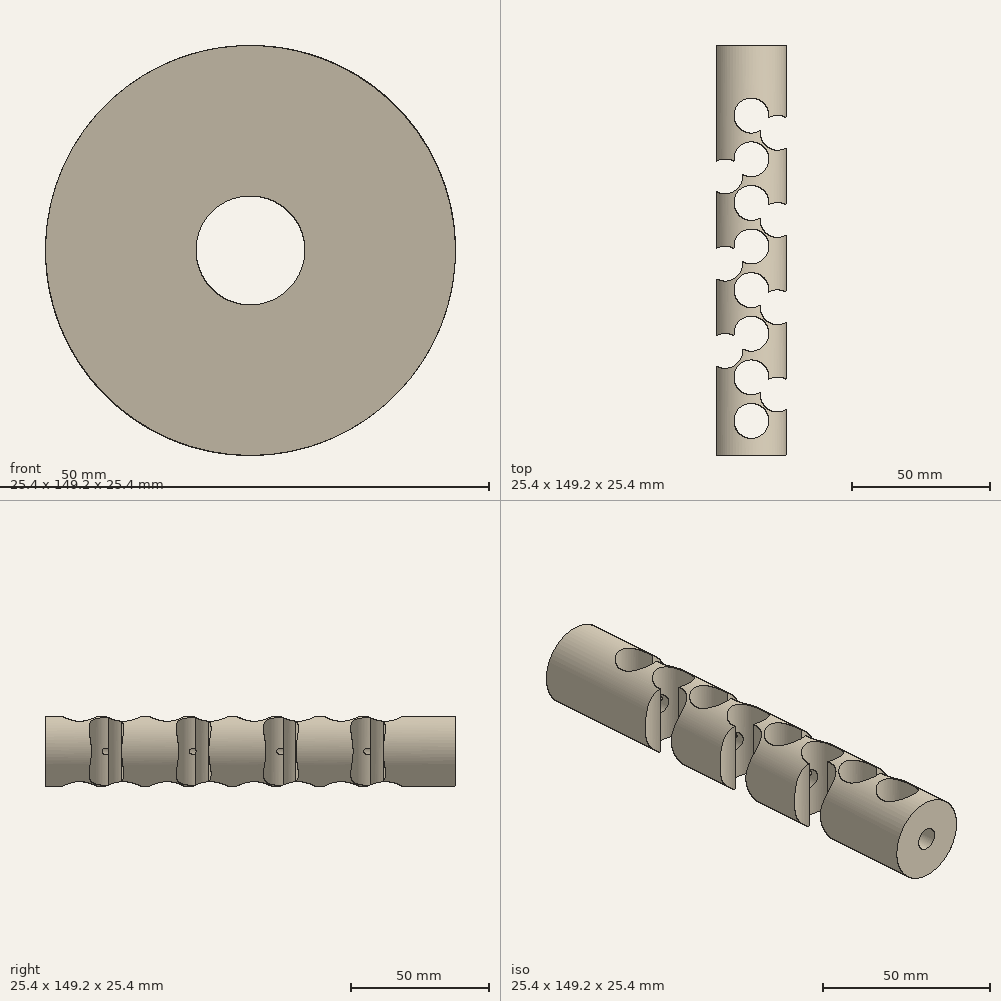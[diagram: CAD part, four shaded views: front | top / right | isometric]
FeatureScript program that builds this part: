
annotation { "Feature Type Name" : "Feature", "Feature Type Description" : "" }
export const myFeature = defineFeature(function(context is Context, id is Id, definition is map)
    precondition{}
    {
        {
            var Q0;
            Q0=qCreatedBy(makeId("Front.planeOp"),FACE);
            var sketch = newSketch(context, id + "F0", { "sketchPlane" : qUnion([Q0])});
            skCircle(sketch, "E0", {"center": v(0, 0) * mm, "radius": 12.7 * mm});
            skSolve(sketch);
        }
        {
            var Q0;
            Q0=makeQuery(id+"F0.imprint","IMPRINT",FACE,{"disambiguationData":[TD([[makeQuery(id+"F0.imprint","IMPRINT",EDGE,{"derivedFrom":sQuery(id+"F0.wireOp",EDGE,"E0")}),1.0]])]});
            extrude(context, id + "F1", {"entities" : qUnion([Q0]), "endBound" : BoundingType.SYMMETRIC, "depth" : 149.22 * mm, "offsetDistance" : 25.4 * mm});
        }
        {
            var Q0;
            Q0=makeQuery(id+"F1.opExtrude","CAP_FACE",FACE,{"disambiguationData":[OSD([sQuery(id+"F0.wireOp",EDGE,"E0")])],"isStart":false});
            var sketch = newSketch(context, id + "F2", { "sketchPlane" : qUnion([Q0])});
            skPoint(sketch, "E1", {"position": v(0, 0) * mm});
            skSolve(sketch);
        }
        {
            var Q0;
            Q0=sQuery(id+"F2.wireOp",VERTEX,"E1");
            var Q1;
            Q1=makeQuery(id+"F1.opExtrude","SWEPT_BODY",BODY,{"disambiguationData":[OSD([sQuery(id+"F0.wireOp",EDGE,"E0")])]});
            hole(context, id + "F3", {"style" : HoleStyle.SIMPLE, "endStyle" : HoleEndStyle.THROUGH, "holeDiameter" : 6.75 * mm, "majorDiameter" : 6.35 * mm, "isTappedThrough" : true, "tappedDepth" : 12.7 * mm, "tapClearance" : 3, "locations" : qUnion([Q0]), "scope" : qUnion([Q1])});
        }
        {
            var Q0;
            Q0=qCreatedBy(makeId("Top.planeOp"),FACE);
            var sketch = newSketch(context, id + "F4", { "sketchPlane" : qUnion([Q0])});
            skLineSegment(sketch, "E2", {"start": v(0, 74.46) * mm, "end": v(0, 49.06) * mm});
            skLineSegment(sketch, "E3", {"start": v(0, 49.06) * mm, "end": v(0, 33.19) * mm});
            skLineSegment(sketch, "E4", {"start": v(0, 33.19) * mm, "end": v(0, 17.31) * mm});
            skLineSegment(sketch, "E5", {"start": v(0, 17.31) * mm, "end": v(0, 1.44) * mm});
            skLineSegment(sketch, "E6", {"start": v(0, 1.44) * mm, "end": v(0, -14.44) * mm});
            skLineSegment(sketch, "E7", {"start": v(0, -14.44) * mm, "end": v(0, -30.31) * mm});
            skLineSegment(sketch, "E8", {"start": v(0, -30.31) * mm, "end": v(0, -46.19) * mm});
            skLineSegment(sketch, "E9", {"start": v(0, -46.19) * mm, "end": v(0, -62.06) * mm});
            skLineSegment(sketch, "E10", {"start": v(0, -62.06) * mm, "end": v(0, -74.72) * mm});
            skSolve(sketch);
        }
        {
            var Q0;
            Q0=sQuery(id+"F4.wireOp",VERTEX,"E9.end");
            var Q1;
            Q1=sQuery(id+"F4.wireOp",VERTEX,"E8.end");
            var Q2;
            Q2=sQuery(id+"F4.wireOp",VERTEX,"E7.end");
            var Q3;
            Q3=sQuery(id+"F4.wireOp",VERTEX,"E6.end");
            var Q4;
            Q4=sQuery(id+"F4.wireOp",VERTEX,"E5.end");
            var Q5;
            Q5=sQuery(id+"F4.wireOp",VERTEX,"E4.end");
            var Q6;
            Q6=sQuery(id+"F4.wireOp",VERTEX,"E3.end");
            var Q7;
            Q7=sQuery(id+"F4.wireOp",VERTEX,"E2.end");
            var Q8;
            Q8=makeQuery(id+"F1.opExtrude","SWEPT_BODY",BODY,{"disambiguationData":[OSD([sQuery(id+"F0.wireOp",EDGE,"E0")])]});
            hole(context, id + "F5", {"style" : HoleStyle.SIMPLE, "endStyle" : HoleEndStyle.BLIND, "holeDiameter" : 12.7 * mm, "majorDiameter" : 6.35 * mm, "holeDepth" : 12.7 * mm, "isTappedThrough" : true, "tappedDepth" : 12.7 * mm, "tapClearance" : 3, "startFromSketch" : true, "locations" : qUnion([Q0, Q1, Q2, Q3, Q4, Q5, Q6, Q7]), "scope" : qUnion([Q8])});
        }
        {
            var Q0;
            Q0=sQuery(id+"F4.wireOp",VERTEX,"E9.end");
            var Q1;
            Q1=sQuery(id+"F4.wireOp",VERTEX,"E8.end");
            var Q2;
            Q2=sQuery(id+"F4.wireOp",VERTEX,"E7.end");
            var Q3;
            Q3=sQuery(id+"F4.wireOp",VERTEX,"E6.end");
            var Q4;
            Q4=sQuery(id+"F4.wireOp",VERTEX,"E5.end");
            var Q5;
            Q5=sQuery(id+"F4.wireOp",VERTEX,"E4.end");
            var Q6;
            Q6=sQuery(id+"F4.wireOp",VERTEX,"E3.end");
            var Q7;
            Q7=sQuery(id+"F4.wireOp",VERTEX,"E2.end");
            var Q8;
            Q8=makeQuery(id+"F1.opExtrude","SWEPT_BODY",BODY,{"disambiguationData":[OSD([sQuery(id+"F0.wireOp",EDGE,"E0")])]});
            hole(context, id + "F6", {"style" : HoleStyle.SIMPLE, "endStyle" : HoleEndStyle.BLIND, "oppositeDirection" : true, "holeDiameter" : 12.7 * mm, "majorDiameter" : 6.35 * mm, "holeDepth" : 12.7 * mm, "isTappedThrough" : true, "tappedDepth" : 12.7 * mm, "tapClearance" : 3, "startFromSketch" : true, "locations" : qUnion([Q0, Q1, Q2, Q3, Q4, Q5, Q6, Q7]), "scope" : qUnion([Q8])});
        }
        {
            var Q0;
            Q0=qCreatedBy(makeId("Top.planeOp"),FACE);
            var sketch = newSketch(context, id + "F7", { "sketchPlane" : qUnion([Q0])});
            skLineSegment(sketch, "E11", {"start": v(0, 49.18) * mm, "end": v(9.53, 49.18) * mm});
            skLineSegment(sketch, "E12", {"start": v(9.53, 49.18) * mm, "end": v(9.53, 42.83) * mm});
            skPoint(sketch, "E13", {"position": v(9.53, 42.83) * mm});
            skLineSegment(sketch, "E14", {"start": v(9.53, 42.83) * mm, "end": v(9.53, 26.95) * mm});
            skLineSegment(sketch, "E15", {"start": v(9.53, 26.95) * mm, "end": v(9.53, 11.08) * mm});
            skLineSegment(sketch, "E16", {"start": v(9.53, 11.08) * mm, "end": v(9.53, -4.8) * mm});
            skLineSegment(sketch, "E17", {"start": v(9.53, -4.8) * mm, "end": v(9.53, -20.67) * mm});
            skLineSegment(sketch, "E18", {"start": v(9.53, -20.67) * mm, "end": v(9.53, -36.55) * mm});
            skLineSegment(sketch, "E19", {"start": v(9.53, -36.55) * mm, "end": v(9.53, -52.42) * mm});
            skLineSegment(sketch, "E20", {"start": v(9.53, 26.95) * mm, "end": v(-9.52, 26.95) * mm});
            skLineSegment(sketch, "E21", {"start": v(9.53, -4.8) * mm, "end": v(-9.52, -4.8) * mm});
            skLineSegment(sketch, "E22", {"start": v(9.53, -36.55) * mm, "end": v(-9.52, -36.55) * mm});
            skSolve(sketch);
        }
        {
            var Q0;
            Q0=sQuery(id+"F7.wireOp",VERTEX,"E13");
            var Q1;
            Q1=sQuery(id+"F7.wireOp",VERTEX,"E15.end");
            var Q2;
            Q2=sQuery(id+"F7.wireOp",VERTEX,"E17.end");
            var Q3;
            Q3=sQuery(id+"F7.wireOp",VERTEX,"E19.end");
            var Q4;
            Q4=makeQuery(id+"F1.opExtrude","SWEPT_BODY",BODY,{"disambiguationData":[OSD([sQuery(id+"F0.wireOp",EDGE,"E0")])]});
            hole(context, id + "F8", {"style" : HoleStyle.SIMPLE, "endStyle" : HoleEndStyle.BLIND, "oppositeDirection" : true, "holeDiameter" : 12.7 * mm, "majorDiameter" : 6.35 * mm, "holeDepth" : 12.7 * mm, "isTappedThrough" : true, "tappedDepth" : 12.7 * mm, "tapClearance" : 3, "startFromSketch" : true, "locations" : qUnion([Q0, Q1, Q2, Q3]), "scope" : qUnion([Q4])});
        }
        {
            var Q0;
            Q0=sQuery(id+"F7.wireOp",VERTEX,"E13");
            var Q1;
            Q1=sQuery(id+"F7.wireOp",VERTEX,"E15.end");
            var Q2;
            Q2=sQuery(id+"F7.wireOp",VERTEX,"E17.end");
            var Q3;
            Q3=sQuery(id+"F7.wireOp",VERTEX,"E19.end");
            var Q4;
            Q4=makeQuery(id+"F1.opExtrude","SWEPT_BODY",BODY,{"disambiguationData":[OSD([sQuery(id+"F0.wireOp",EDGE,"E0")])]});
            hole(context, id + "F9", {"style" : HoleStyle.SIMPLE, "endStyle" : HoleEndStyle.BLIND, "holeDiameter" : 12.7 * mm, "majorDiameter" : 6.35 * mm, "holeDepth" : 12.7 * mm, "isTappedThrough" : true, "tappedDepth" : 12.7 * mm, "tapClearance" : 3, "startFromSketch" : true, "locations" : qUnion([Q0, Q1, Q2, Q3]), "scope" : qUnion([Q4])});
        }
        {
            var Q0;
            Q0=sQuery(id+"F7.wireOp",VERTEX,"E20.end");
            var Q1;
            Q1=sQuery(id+"F7.wireOp",VERTEX,"E21.end");
            var Q2;
            Q2=sQuery(id+"F7.wireOp",VERTEX,"E22.end");
            var Q3;
            Q3=makeQuery(id+"F1.opExtrude","SWEPT_BODY",BODY,{"disambiguationData":[OSD([sQuery(id+"F0.wireOp",EDGE,"E0")])]});
            hole(context, id + "F10", {"style" : HoleStyle.SIMPLE, "endStyle" : HoleEndStyle.BLIND, "oppositeDirection" : true, "holeDiameter" : 12.7 * mm, "majorDiameter" : 6.35 * mm, "holeDepth" : 12.7 * mm, "isTappedThrough" : true, "tappedDepth" : 12.7 * mm, "tapClearance" : 3, "startFromSketch" : true, "locations" : qUnion([Q0, Q1, Q2]), "scope" : qUnion([Q3])});
        }
        {
            var Q0;
            Q0=sQuery(id+"F7.wireOp",VERTEX,"E20.end");
            var Q1;
            Q1=sQuery(id+"F7.wireOp",VERTEX,"E21.end");
            var Q2;
            Q2=sQuery(id+"F7.wireOp",VERTEX,"E22.end");
            var Q3;
            Q3=makeQuery(id+"F1.opExtrude","SWEPT_BODY",BODY,{"disambiguationData":[OSD([sQuery(id+"F0.wireOp",EDGE,"E0")])]});
            hole(context, id + "F11", {"style" : HoleStyle.SIMPLE, "endStyle" : HoleEndStyle.BLIND, "holeDiameter" : 12.7 * mm, "majorDiameter" : 6.35 * mm, "holeDepth" : 12.7 * mm, "isTappedThrough" : true, "tappedDepth" : 12.7 * mm, "tapClearance" : 3, "startFromSketch" : true, "locations" : qUnion([Q0, Q1, Q2]), "scope" : qUnion([Q3])});
        }
    });
